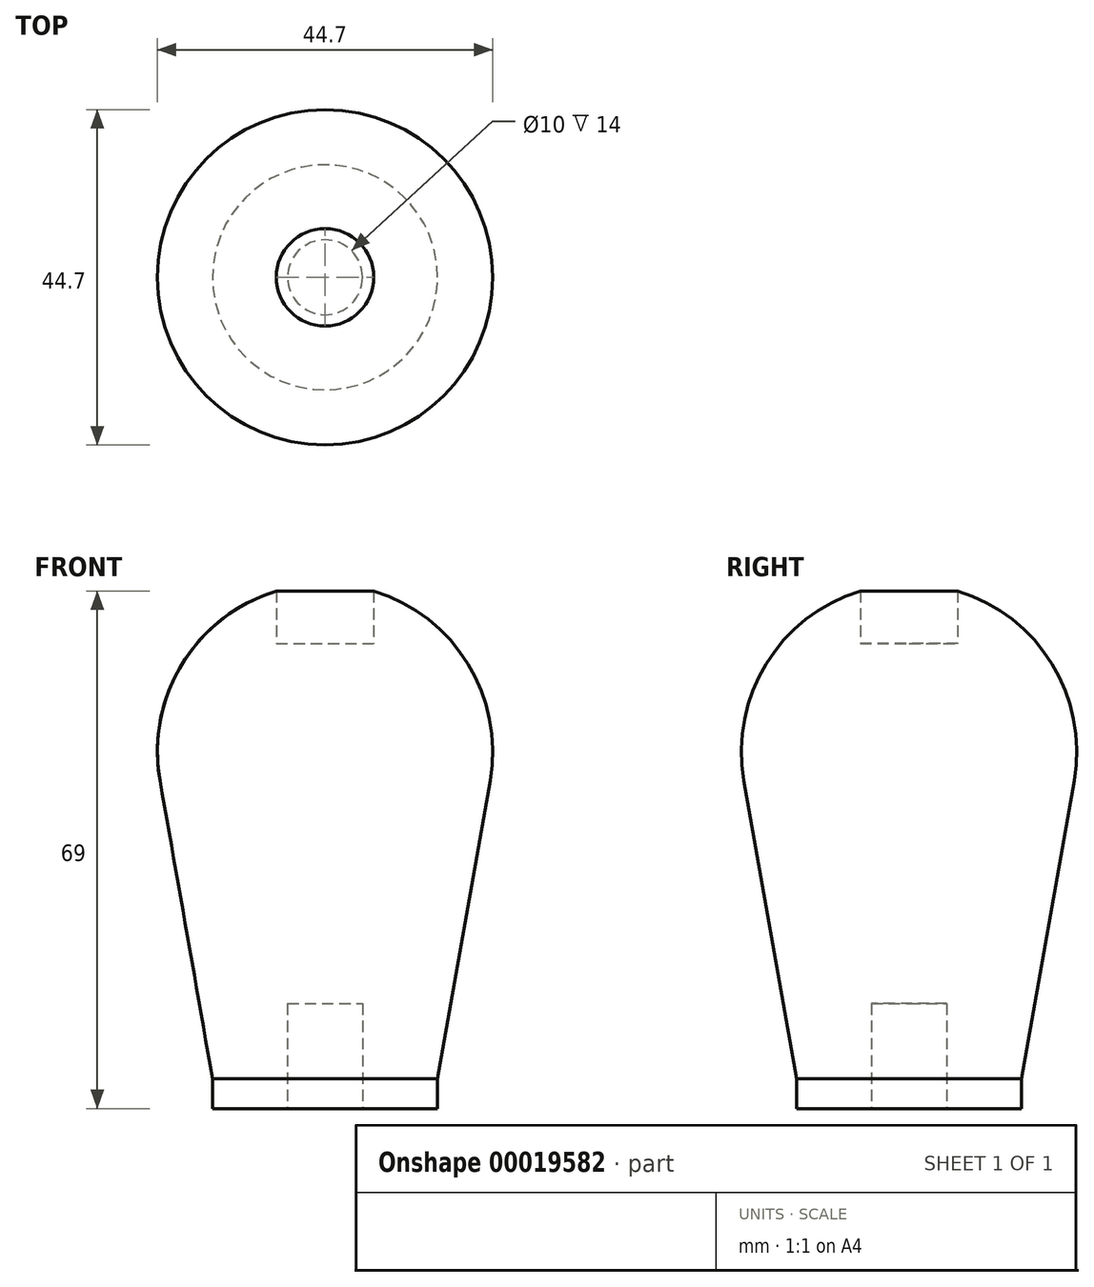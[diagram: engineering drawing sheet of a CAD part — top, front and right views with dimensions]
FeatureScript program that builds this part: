
annotation { "Feature Type Name" : "Feature", "Feature Type Description" : "" }
export const myFeature = defineFeature(function(context is Context, id is Id, definition is map)
    precondition{}
    {
        {
            var Q0;
            Q0=qCreatedBy(makeId("Front.planeOp"),FACE);
            var sketch = newSketch(context, id + "F0", { "sketchPlane" : qUnion([Q0])});
            skLineSegment(sketch, "E0", {"start": v(0, 0) * mm, "end": v(0, 58) * mm});
            skLineSegment(sketch, "E1", {"start": v(0, 58) * mm, "end": v(6.5, 58) * mm});
            skLineSegment(sketch, "E2", {"start": v(6.5, 58) * mm, "end": v(6.5, 65) * mm});
            skArc(sketch, "E3", {"start": v(22, 39.74) * mm, "mid": v(19.04, 55.31) * mm, "end": v(6.5, 65) * mm});
            skLineSegment(sketch, "E4", {"start": v(22, 39.74) * mm, "end": v(15, 0) * mm});
            skLineSegment(sketch, "E5", {"start": v(15, 0) * mm, "end": v(5, 0) * mm});
            skLineSegment(sketch, "E6", {"start": v(5, 0) * mm, "end": v(5, 10) * mm});
            skLineSegment(sketch, "E7", {"start": v(5, 10) * mm, "end": v(0, 10) * mm});
            skLineSegment(sketch, "E8", {"start": v(0, 10) * mm, "end": v(0, 58) * mm});
            skSolve(sketch);
        }
        {
            var Q0;
            Q0=makeQuery(id+"F0.imprint","IMPRINT",FACE,{"disambiguationData":[TD([[makeQuery(id+"F0.imprint","IMPRINT",EDGE,{"derivedFrom":sQuery(id+"F0.wireOp",EDGE,"E1")}),-1.0]])]});
            var Q1;
            Q1=sQuery(id+"F0.wireOp",EDGE,"E0");
            revolve(context, id + "F1", {"surfaceOperationType" : NewSurfaceOperationType.NEW, "entities" : qUnion([Q0]), "axis" : qUnion([Q1]), "revolveType" : RevolveType.FULL});
        }
        {
            var Q0;
            Q0=makeQuery(id+"F1.opRevolve","SWEPT_FACE",FACE,{"disambiguationData":[OSD([sQuery(id+"F0.wireOp",EDGE,"E5")])]});
            var sketch = newSketch(context, id + "F2", { "sketchPlane" : qUnion([Q0])});
            skCircle(sketch, "E9", {"center": v(0, 0) * mm, "radius": 15 * mm});
            skCircle(sketch, "E10", {"center": v(0, 0) * mm, "radius": 5 * mm});
            skSolve(sketch);
        }
        {
            var Q0;
            Q0 = qSketchRegion(id + "F2", true);
            extrude(context, id + "F3", {"entities" : qUnion([Q0]), "operationType" : NewBodyOperationType.ADD, "depth" : 4 * mm, "offsetDistance" : 25 * mm});
        }
    });
